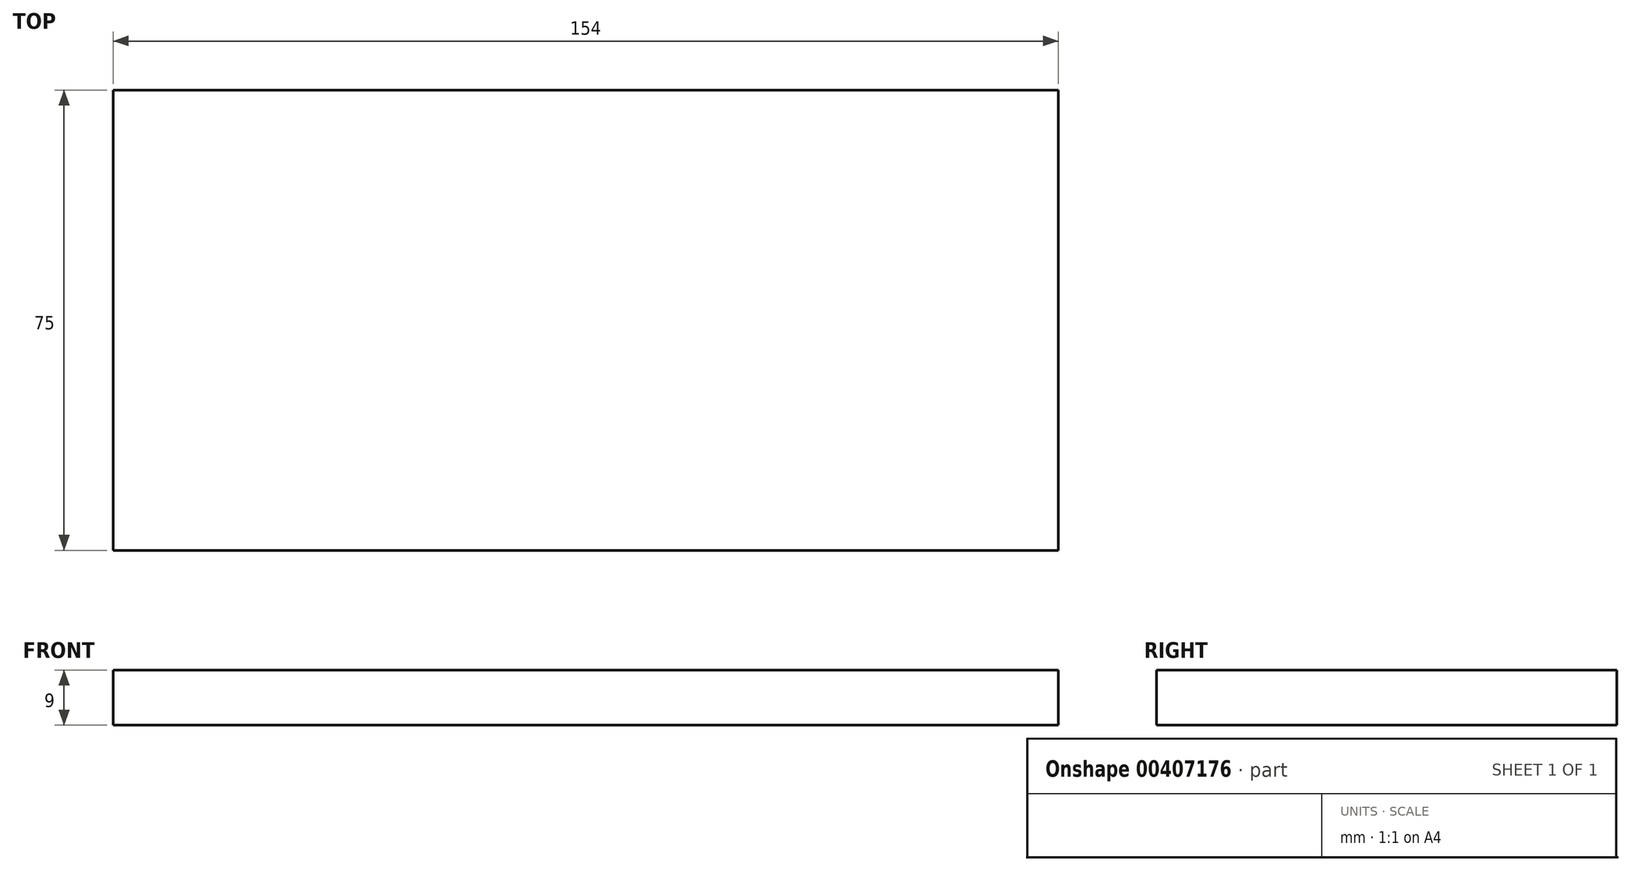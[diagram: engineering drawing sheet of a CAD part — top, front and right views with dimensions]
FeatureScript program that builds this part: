
annotation { "Feature Type Name" : "Feature", "Feature Type Description" : "" }
export const myFeature = defineFeature(function(context is Context, id is Id, definition is map)
    precondition{}
    {
        {
            var Q0;
            Q0=qCreatedBy(makeId("Top.planeOp"),FACE);
            var sketch = newSketch(context, id + "F0", { "sketchPlane" : qUnion([Q0])});
            skLineSegment(sketch, "E0.bottom", {"start": v(77, 37.5) * mm, "end": v(-77, 37.5) * mm});
            skLineSegment(sketch, "E0.top", {"start": v(77, -37.5) * mm, "end": v(-77, -37.5) * mm});
            skLineSegment(sketch, "E0.left", {"start": v(77, 37.5) * mm, "end": v(77, -37.5) * mm});
            skLineSegment(sketch, "E0.right", {"start": v(-77, 37.5) * mm, "end": v(-77, -37.5) * mm});
            skPoint(sketch, "E0.middle", {"position": v(0, 0) * mm});
            skSolve(sketch);
        }
        {
            var Q0;
            Q0=qSketchRegion(id+"F0",true);
            extrude(context, id + "F1", {"entities" : qUnion([Q0]), "depth" : 9 * mm});
        }
    });
